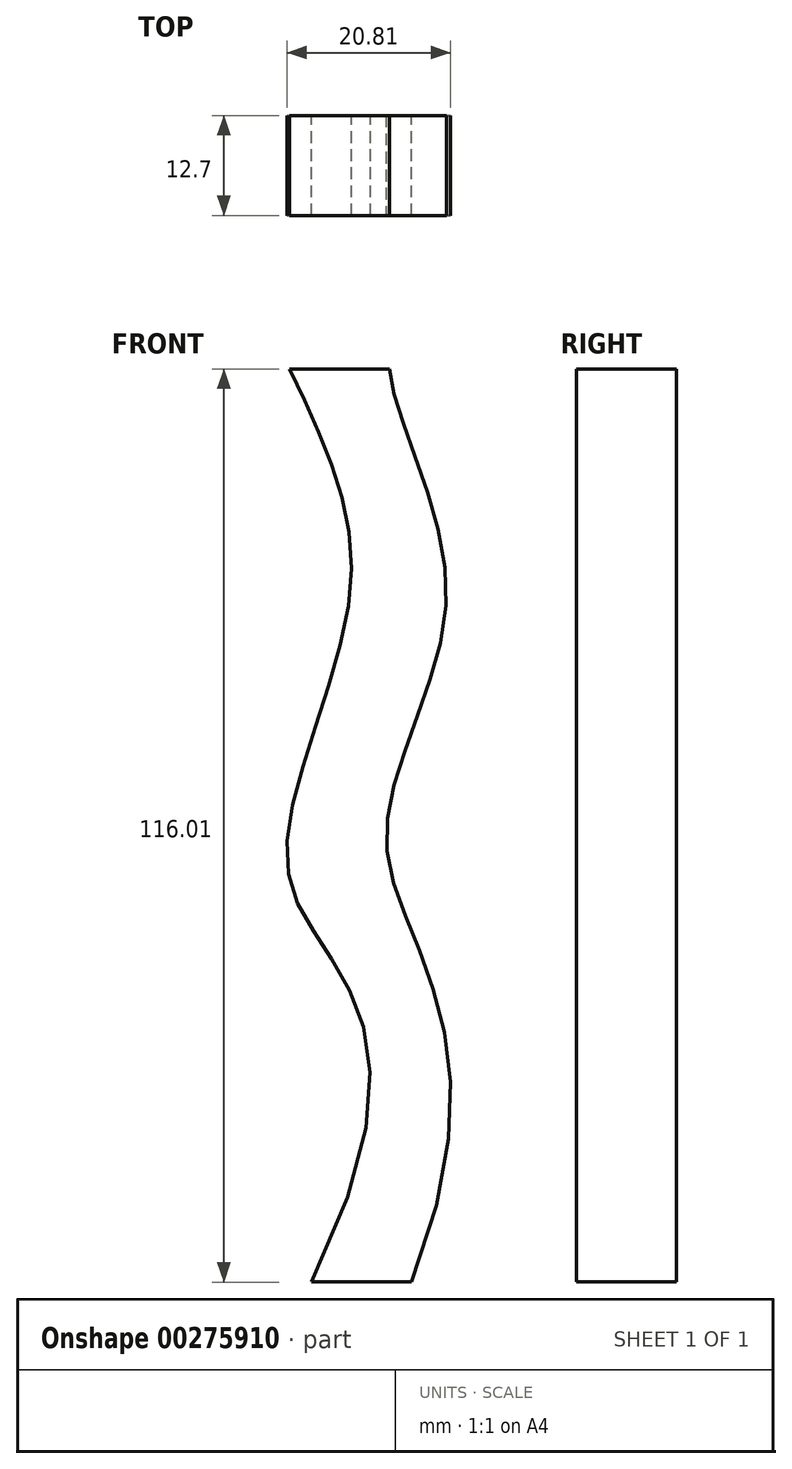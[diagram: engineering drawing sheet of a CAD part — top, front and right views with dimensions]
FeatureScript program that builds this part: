
annotation { "Feature Type Name" : "Feature", "Feature Type Description" : "" }
export const myFeature = defineFeature(function(context is Context, id is Id, definition is map)
    precondition{}
    {
        {
            var Q0;
            Q0=qCreatedBy(makeId("Front.planeOp"),FACE);
            var sketch = newSketch(context, id + "F0", { "sketchPlane" : qUnion([Q0])});
            skLineSegment(sketch, "E0", {"start": v(-19.91, 64.93) * mm, "end": v(-7.21, 64.93) * mm});
            skLineSegment(sketch, "E1", {"start": v(-17.12, -51.08) * mm, "end": v(-4.42, -51.08) * mm});
            skFitSpline(sketch, "E2", {"points": [v(-19.91, 64.93) * mm, v(-12.25, 36.2) * mm, v(-19.91, 0) * mm, v(-17.12, -51.08) * mm], "startDerivative": vector(43.16, -91.21) * mm, "endDerivative": vector(-134.18, -273.83) * mm});
            skFitSpline(sketch, "E3", {"points": [v(-7.21, 64.93) * mm, v(0, 36.2) * mm, v(-7.62, 4.6) * mm, v(-4.42, -51.08) * mm], "startDerivative": vector(4.43, -66.45) * mm, "endDerivative": vector(-93.9, -241) * mm});
            skSolve(sketch);
        }
        {
            var Q0;
            Q0 = qSketchRegion(id + "F0", true);
            extrude(context, id + "F1", {"entities" : qUnion([Q0]), "depth" : 12.7 * mm});
        }
    });
